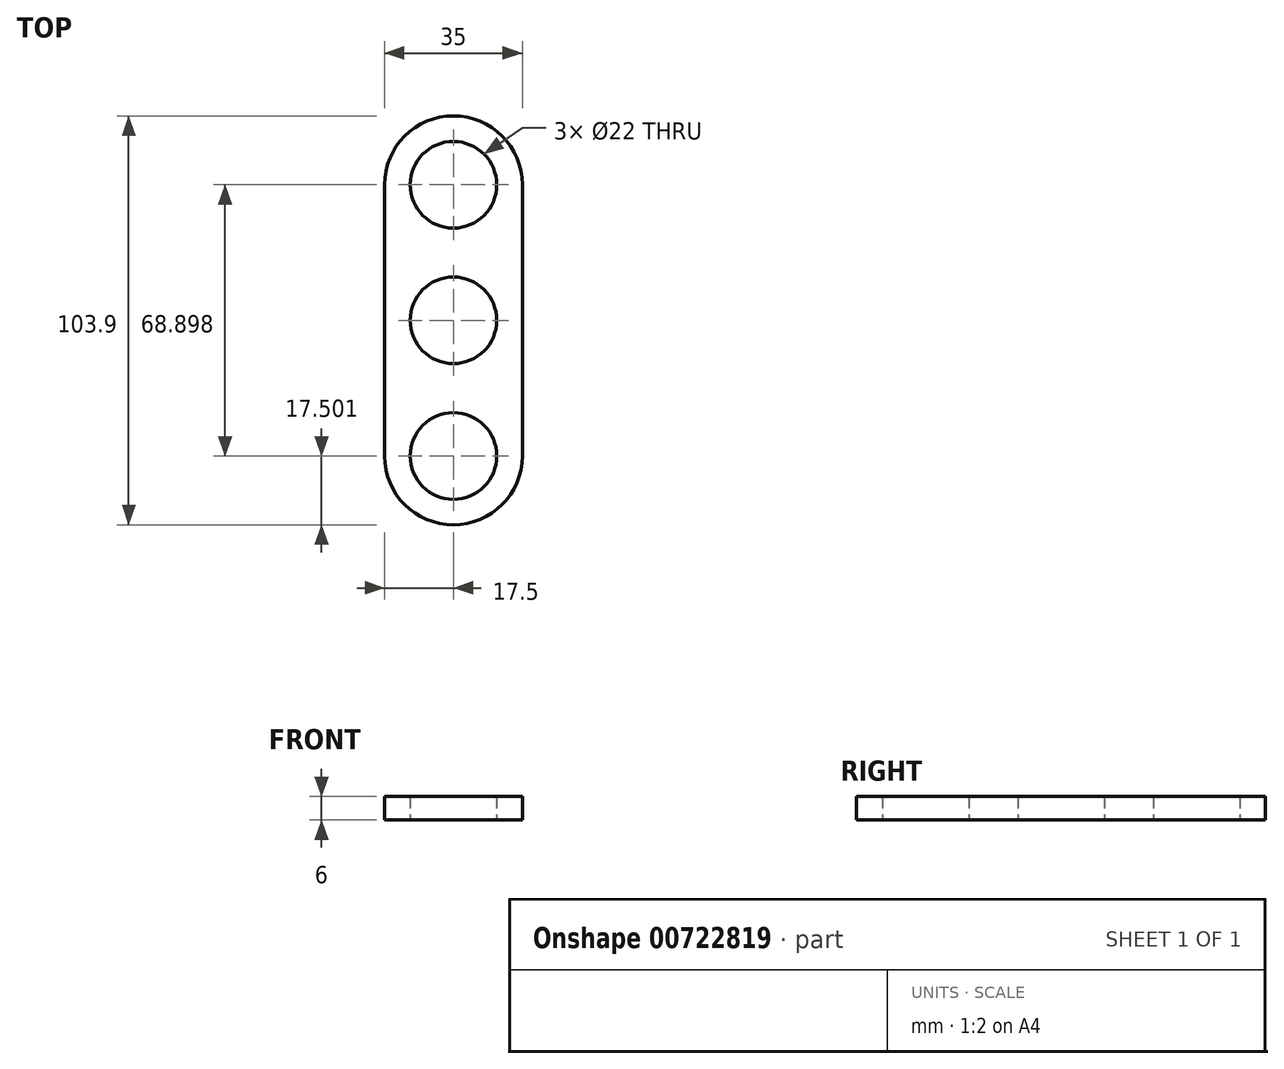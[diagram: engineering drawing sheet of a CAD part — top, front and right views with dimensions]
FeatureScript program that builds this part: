
annotation { "Feature Type Name" : "Feature", "Feature Type Description" : "" }
export const myFeature = defineFeature(function(context is Context, id is Id, definition is map)
    precondition{}
    {
        {
            var Q0;
            Q0=qCreatedBy(makeId("Top.planeOp"),FACE);
            var sketch = newSketch(context, id + "F0", { "sketchPlane" : qUnion([Q0])});
            skArc(sketch, "E0", {"start": v(11, 0) * mm, "mid": v(0, 11) * mm, "end": v(-11, 0) * mm});
            skCircle(sketch, "E1", {"center": v(0, 34.45) * mm, "radius": 11 * mm});
            skArc(sketch, "E2", {"start": v(17.5, 34.45) * mm, "mid": v(0, 51.95) * mm, "end": v(-17.5, 34.45) * mm});
            skLineSegment(sketch, "E3", {"start": v(17.24, -0.7) * mm, "end": v(17.5, 0) * mm});
            skLineSegment(sketch, "E4.MirrorCS", {"start": v(17.24, 0.7) * mm, "end": v(17.5, 0) * mm});
            skArc(sketch, "E5.MirrorCS", {"start": v(11, 0) * mm, "mid": v(0, -11) * mm, "end": v(-11, 0) * mm});
            skArc(sketch, "E6.MirrorCS", {"start": v(17.5, -34.45) * mm, "mid": v(0, -51.95) * mm, "end": v(-17.5, -34.45) * mm});
            skCircle(sketch, "E7.MirrorC", {"center": v(0, -34.45) * mm, "radius": 11 * mm});
            skLineSegment(sketch, "E8", {"start": v(17.5, -34.45) * mm, "end": v(17.5, 34.45) * mm});
            skLineSegment(sketch, "E9", {"start": v(-17.5, 34.45) * mm, "end": v(-17.5, -34.45) * mm});
            skPoint(sketch, "E10.end.orphan", {"position": v(-17.5, 0) * mm});
            skPoint(sketch, "E10.start.orphan", {"position": v(-3.1, 17.22) * mm});
            skPoint(sketch, "E11.trimOffspring.end.orphan", {"position": v(3.1, 17.22) * mm});
            skPoint(sketch, "E12.orphan", {"position": v(3.1, -17.22) * mm});
            skPoint(sketch, "E13.orphan", {"position": v(-3.1, -17.22) * mm});
            skSolve(sketch);
        }
        {
            var Q0;
            Q0 = qSketchRegion(id + "F0", true);
            extrude(context, id + "F1", {"entities" : qUnion([Q0]), "depth" : 6 * mm, "offsetDistance" : 25 * mm});
        }
    });
